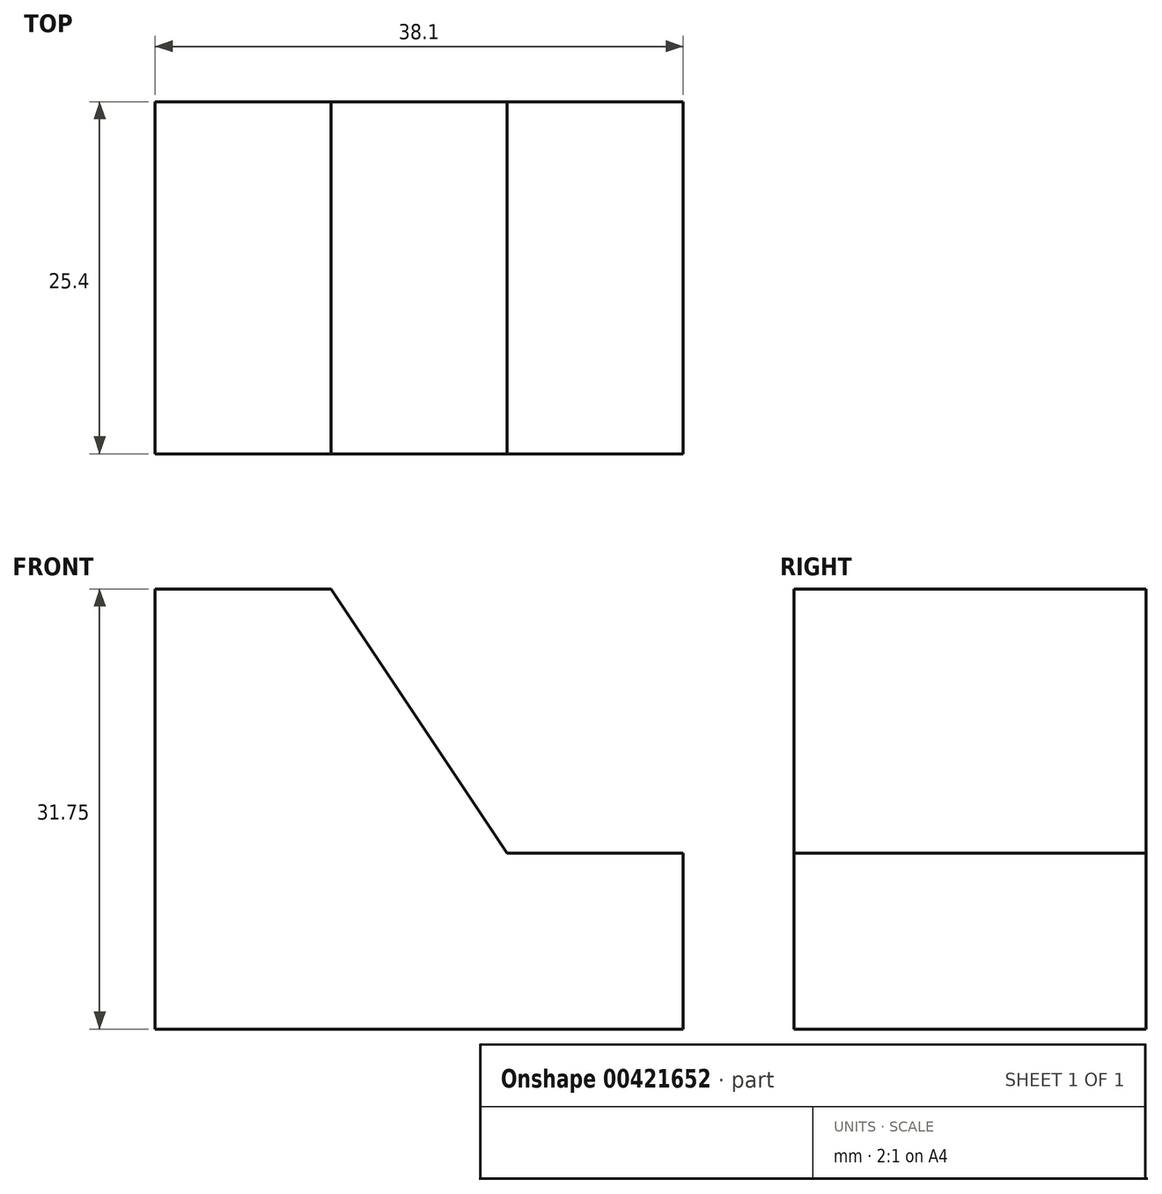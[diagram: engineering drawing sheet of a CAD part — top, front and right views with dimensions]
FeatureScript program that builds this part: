
annotation { "Feature Type Name" : "Feature", "Feature Type Description" : "" }
export const myFeature = defineFeature(function(context is Context, id is Id, definition is map)
    precondition{}
    {
        {
            var Q0;
            Q0=qCreatedBy(makeId("Front.planeOp"),FACE);
            var sketch = newSketch(context, id + "F0", { "sketchPlane" : qUnion([Q0])});
            skLineSegment(sketch, "E0", {"start": v(0, 0) * mm, "end": v(38.1, 0) * mm});
            skLineSegment(sketch, "E1", {"start": v(38.1, 0) * mm, "end": v(38.1, 12.7) * mm});
            skLineSegment(sketch, "E2", {"start": v(0, 0) * mm, "end": v(0, 31.75) * mm});
            skLineSegment(sketch, "E3", {"start": v(0, 31.75) * mm, "end": v(12.7, 31.75) * mm});
            skLineSegment(sketch, "E4", {"start": v(38.1, 12.7) * mm, "end": v(25.4, 12.7) * mm});
            skLineSegment(sketch, "E5", {"start": v(25.4, 12.7) * mm, "end": v(12.7, 31.75) * mm});
            skSolve(sketch);
        }
        {
            var Q0;
            Q0=makeQuery(id+"F0.imprint","IMPRINT",FACE,{"disambiguationData":[TD([[makeQuery(id+"F0.imprint","IMPRINT",EDGE,{"derivedFrom":sQuery(id+"F0.wireOp",EDGE,"E0")}),1.0]])]});
            extrude(context, id + "F1", {"entities" : qUnion([Q0]), "depth" : 25.4 * mm});
        }
    });
